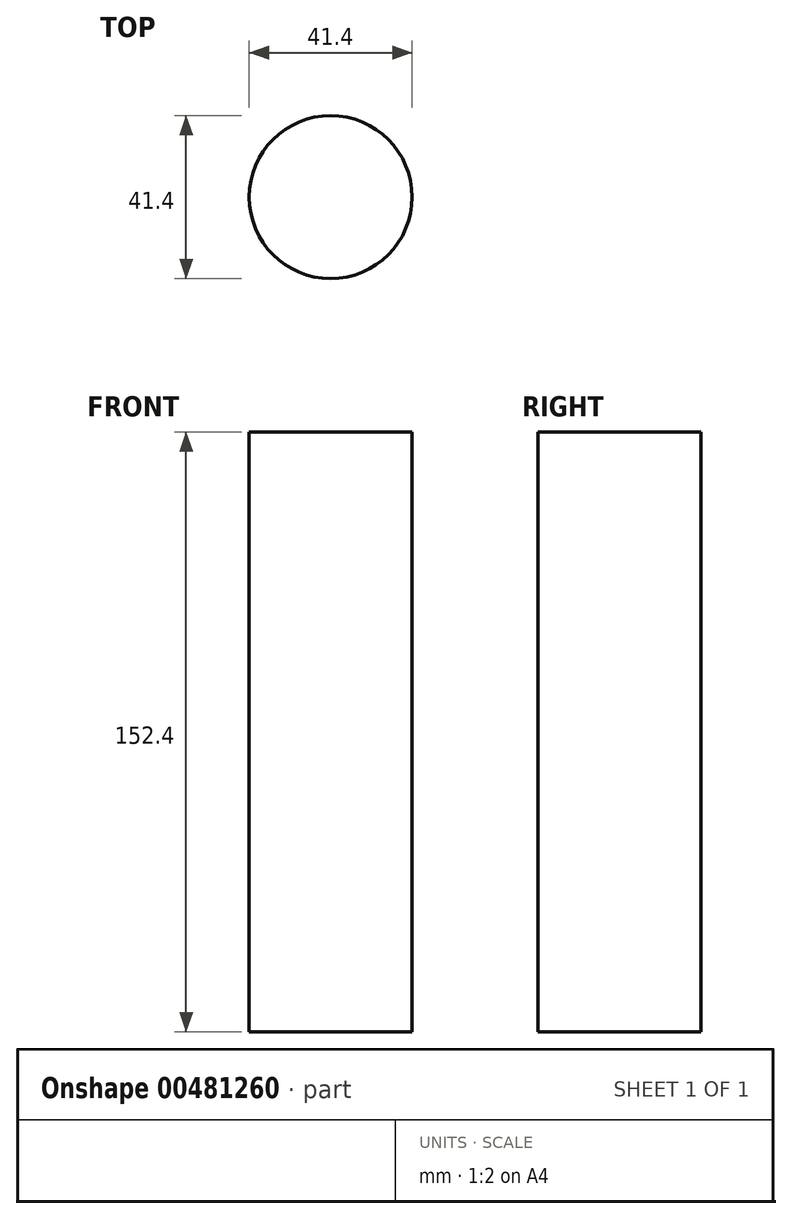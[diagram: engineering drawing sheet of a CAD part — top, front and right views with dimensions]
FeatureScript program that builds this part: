
annotation { "Feature Type Name" : "Feature", "Feature Type Description" : "" }
export const myFeature = defineFeature(function(context is Context, id is Id, definition is map)
    precondition{}
    {
        {
            var Q0;
            Q0=qCreatedBy(makeId("Top.planeOp"),FACE);
            var sketch = newSketch(context, id + "F0", { "sketchPlane" : qUnion([Q0])});
            skCircle(sketch, "E0", {"center": v(0, 0) * mm, "radius": 20.7 * mm});
            skSolve(sketch);
        }
        {
            var Q0;
            Q0=sQuery(id+"F0.wireOp",EDGE,"E0");
            extrude(context, id + "F1", {"bodyType" : ToolBodyType.SURFACE, "surfaceEntities" : qUnion([Q0]), "depth" : 152.4 * mm});
        }
    });
